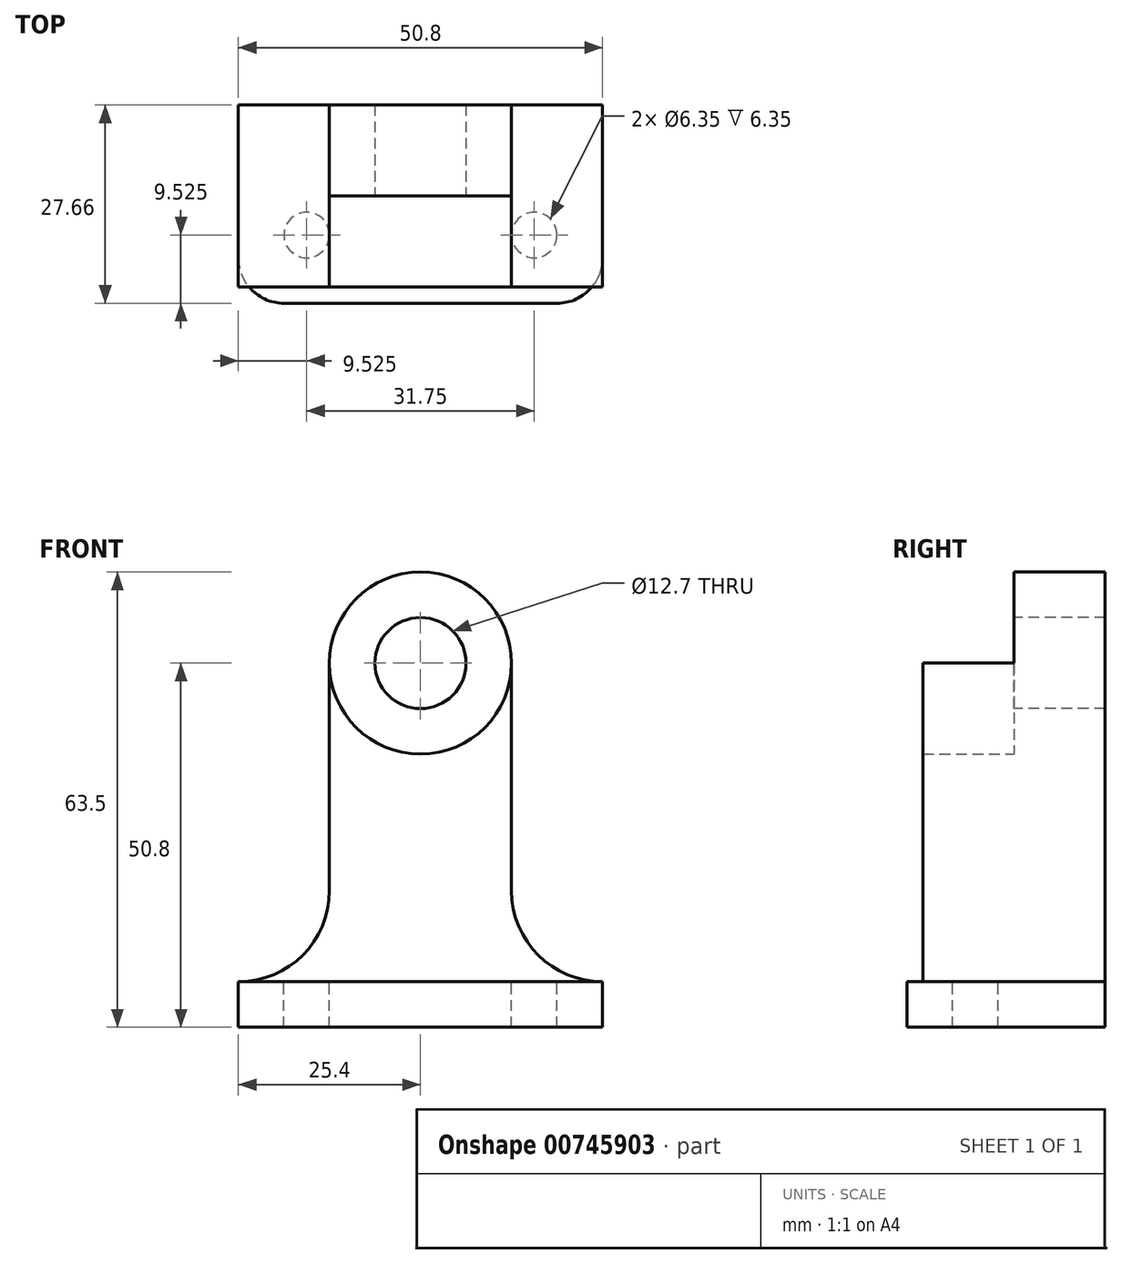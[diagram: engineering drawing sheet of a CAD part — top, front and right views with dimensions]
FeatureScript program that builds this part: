
annotation { "Feature Type Name" : "Feature", "Feature Type Description" : "" }
export const myFeature = defineFeature(function(context is Context, id is Id, definition is map)
    precondition{}
    {
        {
            var Q0;
            Q0=qCreatedBy(makeId("Top.planeOp"),FACE);
            var sketch = newSketch(context, id + "F0", { "sketchPlane" : qUnion([Q0])});
            skLineSegment(sketch, "E0", {"start": v(0, 0) * mm, "end": v(0, 6.35) * mm});
            skLineSegment(sketch, "E1", {"start": v(0, 6.35) * mm, "end": v(-6.35, 6.35) * mm});
            skLineSegment(sketch, "E2", {"start": v(-6.35, 6.35) * mm, "end": v(-6.35, 27.66) * mm});
            skLineSegment(sketch, "E3", {"start": v(-6.35, 27.66) * mm, "end": v(44.45, 27.66) * mm});
            skLineSegment(sketch, "E4", {"start": v(44.45, 27.66) * mm, "end": v(44.45, 6.35) * mm});
            skLineSegment(sketch, "E5", {"start": v(44.45, 6.35) * mm, "end": v(38.1, 6.35) * mm});
            skLineSegment(sketch, "E6", {"start": v(38.1, 6.35) * mm, "end": v(38.1, 0) * mm});
            skLineSegment(sketch, "E7", {"start": v(38.1, 0) * mm, "end": v(0, 0) * mm});
            skArc(sketch, "E8", {"start": v(-6.35, 6.35) * mm, "mid": v(-4.5, 1.86) * mm, "end": v(0, 0) * mm});
            skArc(sketch, "E9", {"start": v(38.1, 0) * mm, "mid": v(42.6, 1.86) * mm, "end": v(44.45, 6.35) * mm});
            skSolve(sketch);
        }
        {
            var Q0;
            Q0=makeQuery(id+"F0.imprint","IMPRINT",FACE,{"disambiguationData":[TD([[makeQuery(id+"F0.imprint","IMPRINT",EDGE,{"derivedFrom":sQuery(id+"F0.wireOp",EDGE,"E0")}),-1.0]])]});
            var Q1;
            Q1=makeQuery(id+"F0.imprint","IMPRINT",FACE,{"disambiguationData":[TD([[makeQuery(id+"F0.imprint","IMPRINT",EDGE,{"derivedFrom":sQuery(id+"F0.wireOp",EDGE,"E0")}),1.0]])]});
            var Q2;
            Q2=makeQuery(id+"F0.imprint","IMPRINT",FACE,{"disambiguationData":[TD([[makeQuery(id+"F0.imprint","IMPRINT",EDGE,{"derivedFrom":sQuery(id+"F0.wireOp",EDGE,"E5")}),1.0]])]});
            extrude(context, id + "F1", {"entities" : qUnion([Q0, Q1, Q2]), "depth" : 6.35 * mm, "offsetDistance" : 25.4 * mm});
        }
        {
            var Q0;
            Q0=makeQuery(id+"F1.opExtrude","CAP_FACE",FACE,{"disambiguationData":[OSD([sQuery(id+"F0.wireOp",EDGE,"E2"),sQuery(id+"F0.wireOp",EDGE,"E3"),sQuery(id+"F0.wireOp",EDGE,"E4"),sQuery(id+"F0.wireOp",EDGE,"E7"),sQuery(id+"F0.wireOp",EDGE,"E8"),sQuery(id+"F0.wireOp",EDGE,"E9")])],"isStart":false});
            var sketch = newSketch(context, id + "F2", { "sketchPlane" : qUnion([Q0])});
            skCircle(sketch, "E10", {"center": v(3.17, 9.53) * mm, "radius": 3.17 * mm});
            skCircle(sketch, "E11", {"center": v(34.93, 9.53) * mm, "radius": 3.18 * mm});
            skSolve(sketch);
        }
        {
            var Q0;
            Q0=makeQuery(id+"F2.imprint","IMPRINT",FACE,{"disambiguationData":[TD([[makeQuery(id+"F2.imprint","IMPRINT",EDGE,{"derivedFrom":sQuery(id+"F2.wireOp",EDGE,"E10")}),1.0]])]});
            var Q1;
            Q1=makeQuery(id+"F2.imprint","IMPRINT",FACE,{"disambiguationData":[TD([[makeQuery(id+"F2.imprint","IMPRINT",EDGE,{"derivedFrom":sQuery(id+"F2.wireOp",EDGE,"E11")}),1.0]])]});
            extrude(context, id + "F3", {"entities" : qUnion([Q0, Q1]), "operationType" : NewBodyOperationType.REMOVE, "oppositeDirection" : true, "depth" : 25.4 * mm, "offsetDistance" : 25.4 * mm});
        }
        {
            var Q0;
            Q0=makeQuery(id+"F1.opExtrude","SWEPT_FACE",FACE,{"disambiguationData":[OSD([sQuery(id+"F0.wireOp",EDGE,"E3")])]});
            var sketch = newSketch(context, id + "F4", { "sketchPlane" : qUnion([Q0])});
            skLineSegment(sketch, "E12", {"start": v(-44.45, 6.35) * mm, "end": v(-44.45, 19.05) * mm});
            skLineSegment(sketch, "E13", {"start": v(-44.45, 19.05) * mm, "end": v(-31.75, 19.05) * mm});
            skLineSegment(sketch, "E14", {"start": v(-31.75, 19.05) * mm, "end": v(-31.75, 50.8) * mm});
            skLineSegment(sketch, "E15", {"start": v(-31.75, 50.8) * mm, "end": v(-6.35, 50.8) * mm});
            skLineSegment(sketch, "E16", {"start": v(-6.35, 50.8) * mm, "end": v(-6.35, 19.05) * mm});
            skLineSegment(sketch, "E17", {"start": v(-6.35, 19.05) * mm, "end": v(6.35, 19.05) * mm});
            skLineSegment(sketch, "E18", {"start": v(6.35, 19.05) * mm, "end": v(6.35, 6.35) * mm});
            skArc(sketch, "E19", {"start": v(-44.45, 6.35) * mm, "mid": v(-35.47, 10.07) * mm, "end": v(-31.75, 19.05) * mm});
            skArc(sketch, "E20", {"start": v(-6.35, 19.05) * mm, "mid": v(-2.63, 10.07) * mm, "end": v(6.35, 6.35) * mm});
            skCircle(sketch, "E21", {"center": v(-19.05, 50.8) * mm, "radius": 12.7 * mm});
            skSolve(sketch);
        }
        {
            var Q0;
            {var subQ1=sQuery(id+"F4.wireOp",EDGE,"E14");Q0=makeQuery(id+"F4.imprint","IMPRINT",FACE,{"disambiguationData":[TD([[makeQuery(id+"F4.imprint","IMPRINT",EDGE,{"derivedFrom":subQ1}),-1.0]])]});}
            var Q1;
            {var subQ0=sQuery(id+"F4.wireOp",EDGE,"E15");Q1=makeQuery(id+"F4.imprint","IMPRINT",FACE,{"disambiguationData":[TD([[makeQuery(id+"F4.imprint","IMPRINT",EDGE,{"derivedFrom":subQ0}),-1.0]])]});}
            var Q2;
            {var subQ0=sQuery(id+"F4.wireOp",EDGE,"E15");Q2=makeQuery(id+"F4.imprint","IMPRINT",FACE,{"disambiguationData":[TD([[makeQuery(id+"F4.imprint","IMPRINT",EDGE,{"derivedFrom":subQ0}),1.0]])]});}
            extrude(context, id + "F5", {"entities" : qUnion([Q0, Q1, Q2]), "operationType" : NewBodyOperationType.ADD, "oppositeDirection" : true, "depth" : 12.7 * mm, "offsetDistance" : 25.4 * mm});
        }
        {
            var Q0;
            Q0=makeQuery(id+"F5.opExtrude","CAP_FACE",FACE,{"disambiguationData":[OSD([sQuery(id+"F0.wireOp",EDGE,"E3"),sQuery(id+"F4.wireOp",EDGE,"E14"),sQuery(id+"F4.wireOp",EDGE,"E16"),sQuery(id+"F4.wireOp",EDGE,"E19"),sQuery(id+"F4.wireOp",EDGE,"E20"),sQuery(id+"F4.wireOp",EDGE,"E21")])],"isStart":false});
            var sketch = newSketch(context, id + "F6", { "sketchPlane" : qUnion([Q0])});
            skCircle(sketch, "E22", {"center": v(19.05, 50.8) * mm, "radius": 6.35 * mm});
            skSolve(sketch);
        }
        {
            var Q0;
            Q0=makeQuery(id+"F6.imprint","IMPRINT",FACE,{"disambiguationData":[TD([[makeQuery(id+"F6.imprint","IMPRINT",EDGE,{"derivedFrom":sQuery(id+"F6.wireOp",EDGE,"E22")}),1.0]])]});
            var Q1;
            Q1=sQuery(id+"F6.wireOp",EDGE,"E22");
            extrude(context, id + "F7", {"entities" : qUnion([Q0]), "operationType" : NewBodyOperationType.REMOVE, "surfaceEntities" : qUnion([Q1]), "oppositeDirection" : true, "depth" : 25.4 * mm, "offsetDistance" : 25.4 * mm});
        }
        {
            var Q0;
            Q0=makeQuery(id+"F5.opExtrude","CAP_FACE",FACE,{"disambiguationData":[OSD([sQuery(id+"F0.wireOp",EDGE,"E3"),sQuery(id+"F4.wireOp",EDGE,"E14"),sQuery(id+"F4.wireOp",EDGE,"E16"),sQuery(id+"F4.wireOp",EDGE,"E19"),sQuery(id+"F4.wireOp",EDGE,"E20"),sQuery(id+"F4.wireOp",EDGE,"E21")])],"isStart":false});
            var sketch = newSketch(context, id + "F8", { "sketchPlane" : qUnion([Q0])});
            skCircle(sketch, "E23", {"center": v(19.05, 50.8) * mm, "radius": 12.7 * mm});
            skSolve(sketch);
        }
        {
            var Q0;
            {var subQ0=sQuery(id+"F8.wireOp",EDGE,"E23");Q0=makeQuery(id+"F8.imprint","IMPRINT",FACE,{"disambiguationData":[TD([[makeQuery(id+"F8.imprint","IMPRINT",EDGE,{"disambiguationData":[OD(0.0)],"derivedFrom":subQ0}),-1.0]])]});}
            extrude(context, id + "F9", {"entities" : qUnion([Q0]), "operationType" : NewBodyOperationType.ADD, "depth" : 12.7 * mm, "offsetDistance" : 25.4 * mm});
        }
    });
